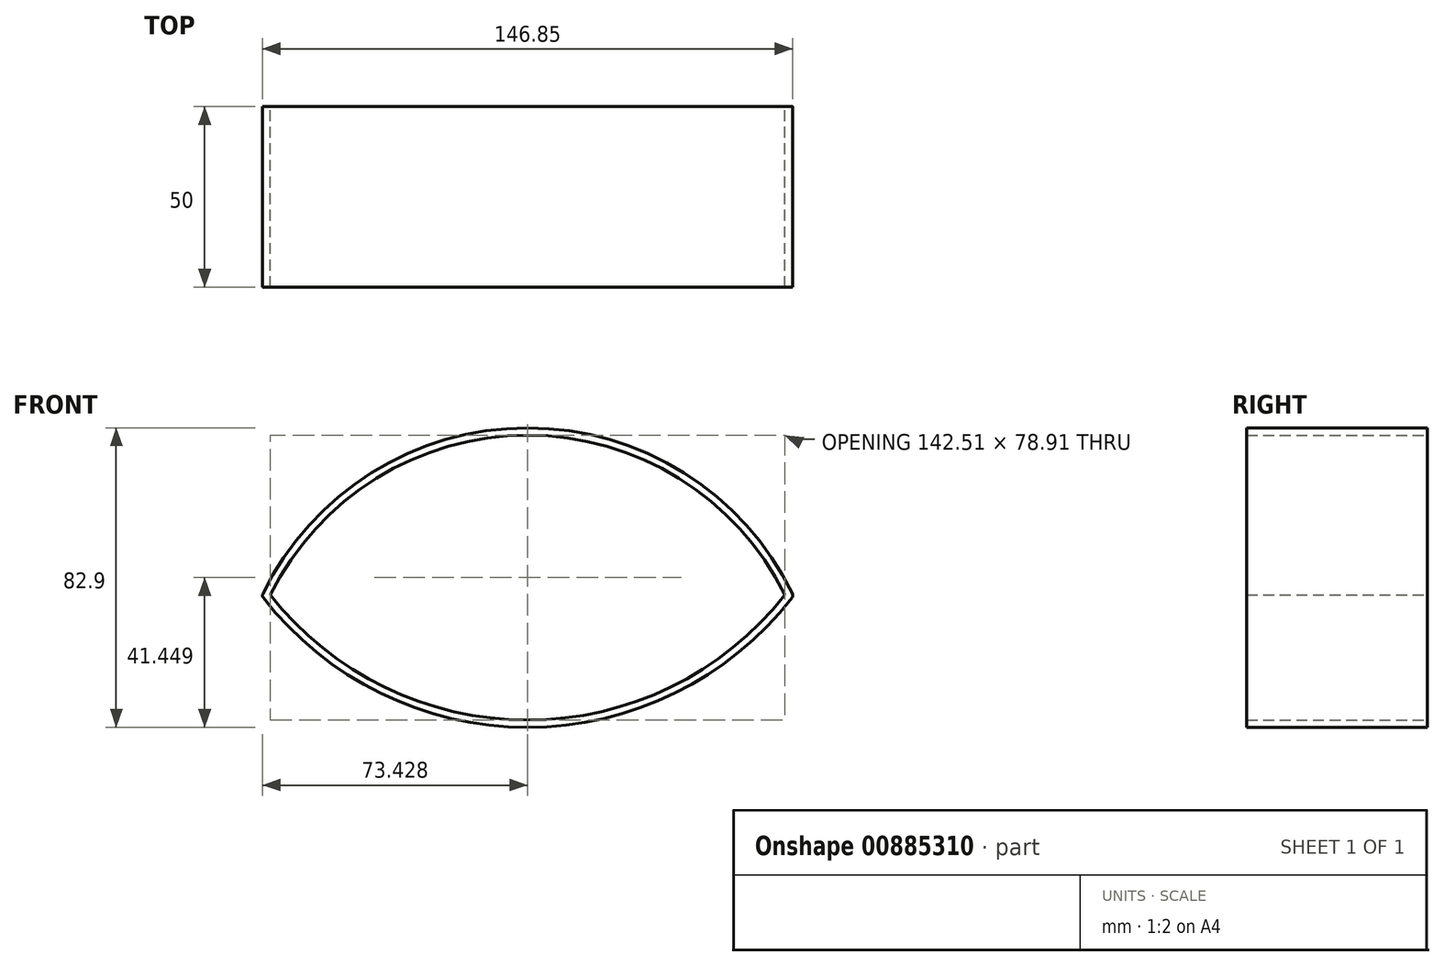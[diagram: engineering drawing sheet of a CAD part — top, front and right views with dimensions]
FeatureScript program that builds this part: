
annotation { "Feature Type Name" : "Feature", "Feature Type Description" : "" }
export const myFeature = defineFeature(function(context is Context, id is Id, definition is map)
    precondition{}
    {
        {
            var Q0;
            Q0=qCreatedBy(makeId("Front.planeOp"),FACE);
            var sketch = newSketch(context, id + "F0", { "sketchPlane" : qUnion([Q0])});
            skArc(sketch, "E0.0.startCap", {"start": v(74.46, 0.44) * mm, "mid": v(74.56, -0.1) * mm, "end": v(74.35, -0.61) * mm});
            skArc(sketch, "E0.0.endCap", {"start": v(-70.67, -0.79) * mm, "mid": v(-71.92, -0.78) * mm, "end": v(-72.19, 0.44) * mm});
            skArc(sketch, "E0.0.left", {"start": v(72.4, 0.12) * mm, "mid": v(1.14, 44.4) * mm, "end": v(-70.12, 0.12) * mm});
            skArc(sketch, "E0.0.right", {"start": v(74.46, 0.44) * mm, "mid": v(1.14, 46.4) * mm, "end": v(-72.19, 0.44) * mm});
            skArc(sketch, "E1.0.startCap", {"start": v(-72.08, -0.61) * mm, "mid": v(-72.06, 0.63) * mm, "end": v(-70.85, 0.9) * mm});
            skArc(sketch, "E1.0.left", {"start": v(-70.12, 0.12) * mm, "mid": v(1.14, -34.51) * mm, "end": v(72.4, 0.12) * mm});
            skArc(sketch, "E1.0.right", {"start": v(-72.08, -0.61) * mm, "mid": v(1.14, -36.51) * mm, "end": v(74.35, -0.61) * mm});
            skSolve(sketch);
        }
        {
            var Q0;
            Q0 = qSketchRegion(id + "F0", true);
            extrude(context, id + "F1", {"entities" : qUnion([Q0]), "endBound" : BoundingType.SYMMETRIC, "depth" : 50 * mm, "offsetDistance" : 25 * mm});
        }
    });
